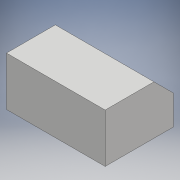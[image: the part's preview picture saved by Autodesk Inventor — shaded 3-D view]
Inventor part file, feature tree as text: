
AUTODESK INVENTOR PART (.ipt)
format: ipt  version: 2018 (Build 220112000, 112)  size: 152,064 bytes
history: native  units: mm
features: sketch x7, extrude x7, plane x3
ambient origin geometry x8: Origin, YZ Plane, XZ Plane, XY Plane, X Axis, Y Axis, Z Axis, Center Point
bodies: Solid1 (feature_tree)
feature tree (17):
  sketch  "Sketch1"  dims[d0=100.0mm d1=50.0mm]
  sketch  "Sketch2"  dims[d2=100.0mm d3=50.0mm]
  sketch  "Sketch3"  dims[d12=1.0mm d13=0.0mm d14=1.0mm d15=0.0mm]
  extrude  "Extrusion1"  Depth=50.0mm
  extrude  "Extrusion2"  Depth=50.0mm
  extrude  "Extrusion3"  Depth=1.0mm TaperAngle=0.0deg
  plane  "Work Plane1"
  extrude  "Extrusion4"  Depth=50.0mm
  plane  "Work Plane2"
  sketch  "Sketch5"  dims[d18=20.0mm d19=30.0mm]
  extrude  "Extrusion5"  Depth=30.0mm
  extrude  "Extrusion6"  Depth=1.0mm TaperAngle=0.0deg
  plane  "Work Plane3"
  extrude  "Extrusion7"  Depth=1.0mm TaperAngle=0.0deg
  sketch  "Sketch4"  dims[d16=50.0mm d17=50.0mm]
  sketch  "Sketch6"  dims[d20=1.0mm d21=1.0mm d22=0.0mm]
  sketch  "Sketch7"  dims[d23=100.0mm d24=1.0mm d25=0.0mm d26=-50.0mm d27=101.0mm d28=70.0mm d29=100.0mm d30=0.0mm d31=1.0mm d32=0.0mm d33=70.0mm d34=1.0mm d35=0.0mm]
